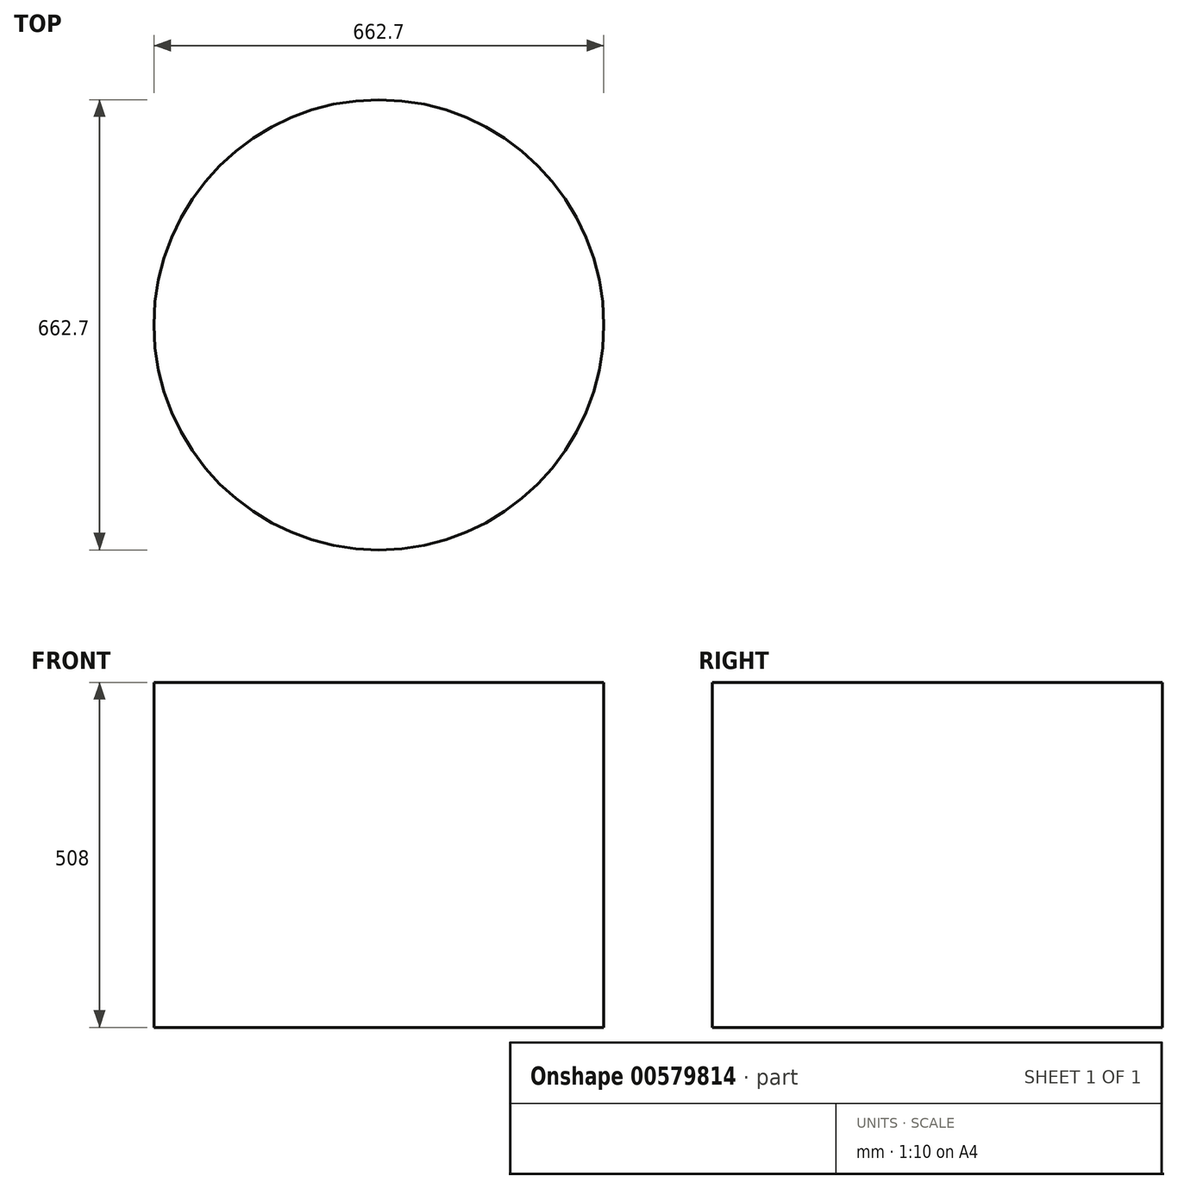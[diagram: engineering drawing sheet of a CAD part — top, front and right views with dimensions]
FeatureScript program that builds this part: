
annotation { "Feature Type Name" : "Feature", "Feature Type Description" : "" }
export const myFeature = defineFeature(function(context is Context, id is Id, definition is map)
    precondition{}
    {
        {
            var Q0;
            Q0=qCreatedBy(makeId("Top.planeOp"),FACE);
            var sketch = newSketch(context, id + "F0", { "sketchPlane" : qUnion([Q0])});
            skCircle(sketch, "E0", {"center": v(0, 0) * mm, "radius": 331.35 * mm});
            skSolve(sketch);
        }
        {
            var Q0;
            Q0 = qSketchRegion(id + "F0", true);
            extrude(context, id + "F1", {"entities" : qUnion([Q0]), "depth" : 508 * mm, "offsetDistance" : 25.4 * mm});
        }
    });
